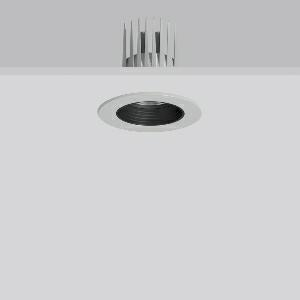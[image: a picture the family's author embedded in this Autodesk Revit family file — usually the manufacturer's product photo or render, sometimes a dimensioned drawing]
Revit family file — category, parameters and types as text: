
# Revit family: heledon_mini_e_901747_004_3_a954
name_source: partatom
category: Lighting Fixtures
units: mm (PartAtom-declared; Revit-internal decimal feet)

## family parameters
Cut with Voids When Loaded = No
Host = Face
Light Source = No
Part Type = Normal
Room Calculation Point = No
Round Connector Dimension = Use Diameter
Shared = No

## types (1)
- HELEDON mini E (1 x LED Modul 935, 1950 lm, 3500)
    Apparent Load = 20 VA
    Approval mark = CE
    CIE Flux Codes = 95 100 100 100 100
    Color Rendering = 92
    Color Temperature = 3500
    Default Elevation = 1800 mm
    Description = Series: HELEDON mini
Round recessed downlight. Housing: die-cast aluminium, powder-coated. Black plastic ring and recessed LED to prevent glare from the side. Optical assembly with lens made of plastic (polycarbonate) for the best homogeneous light distribution - can be changed without tools. Best colour rendering index Ra>90. Suitable for Recessed ceiling mounting. Installation without tools thanks to spring fastening system. Including separate LED converter with connecting cable 600 mm.High quality converter without flickering and stroboscopic effect. Through-wiring box (5 pole) available as accessory. The following accessories can be mounted without use of tools: interchangeable lenses, decorative glasses, honeycomb louvre, clear and frosted diffusers, white interchangeable plastic ring. 
Colour: silver
Diameter: 124 mm
Height: 3 mm
Cut-out diameter: 114 mm
Recess height: 170 mm
Luminaire: recess height: 120 mm
Lamp: LED
Socket: without socket
Colour temperature: 3500K
Colour rendering index (CRI): 92
System power: 20 W
Rated luminous flux: 1950 lm
Luminous efficiency: 98 lm/W
Control gear: Regulated power supply
Protection class: II
Type of protection: IP 20
    Height = 0 mm  [stored 0 ft]
    Lamp = 1 x LED Modul 935
    Lamp Light Flux = 1950 lm
    Lamp count = 1
    Length = 124 mm  [stored 0.406824 ft]
    Lifetime = 50000 h
    Luminous efficacy = 98 lm/W
    Manufacturer = RZB
    ModVariant = No
    Model = 901747.004.3
    Mounting Place = Ceiling
    Mounting Type = Recessed
    Number of Poles = 1
    OnlyDefault = Yes
    Power Factor = 1
    Product Name = HELEDON mini E
    Product group = Recessed downlights
    ProductGroupID = 402
    Protection Class = Protection class II
    Protection Degree = IP 20
    RLX_Detail_Level = 1
    RLX_Emergency_Light_Flux = 0 lm
    RLX_Emergency_Type = 0
    RLX_Emergency_Type_DB = No
    RlxData = <blob elided: 132281 chars, md5=f0b78492>
    Socket = socket
    Standby Power = 0 W
    System Light Flux = 1950 lm
    System Power = 20 W
    Type Comments = Product without accessories
    Type Image = 901656.004.jpg
    URL = http://relux.com
    VarID = ---
    Voltage = 230 V
    Voltage Range = 220-240 V
    Weight = 0.00 kg
    Width = 0 mm  [stored 0 ft]

note: [stored X ft] marks values corroborated as IEEE doubles in the binary element streams (Revit-internal decimal feet)

## geometry (parser evidence)
native form markers: Blend x4, Sweep x11
no freeform markers — native parametric forms only
